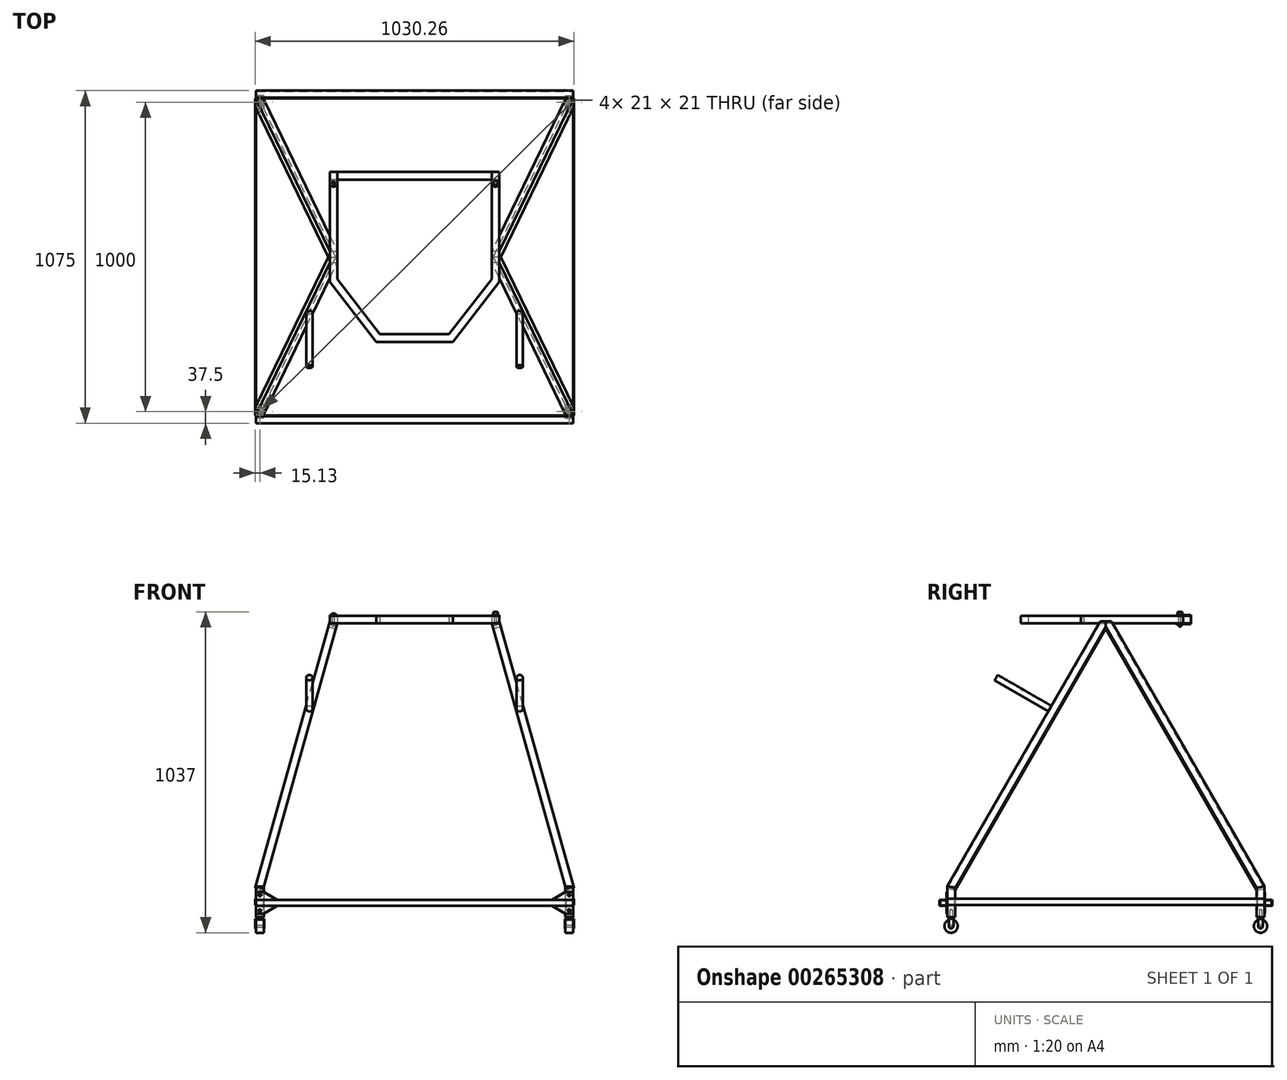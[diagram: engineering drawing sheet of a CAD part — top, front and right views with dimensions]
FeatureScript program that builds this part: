
annotation { "Feature Type Name" : "Feature", "Feature Type Description" : "" }
export const myFeature = defineFeature(function(context is Context, id is Id, definition is map)
    precondition{}
    {
        {
            assignVariable(context, id + "F0", {"name" : "Height", "anyValue" : 1000});
        }
        {
            var Q0;
            Q0=qCreatedBy(makeId("Top.planeOp"),FACE);
            var sketch = newSketch(context, id + "F1", { "sketchPlane" : qUnion([Q0])});
            skLineSegment(sketch, "E0.bottom", {"start": v(-487.5, 487.5) * mm, "end": v(-512.5, 487.5) * mm});
            skLineSegment(sketch, "E0.top", {"start": v(-487.5, 512.5) * mm, "end": v(-512.5, 512.5) * mm});
            skLineSegment(sketch, "E0.left", {"start": v(-487.5, 487.5) * mm, "end": v(-487.5, 512.5) * mm});
            skLineSegment(sketch, "E0.right", {"start": v(-512.5, 487.5) * mm, "end": v(-512.5, 512.5) * mm});
            skPoint(sketch, "E0.middle", {"position": v(-500, 500) * mm});
            skLineSegment(sketch, "E1.bottom", {"start": v(-489.5, 489.5) * mm, "end": v(-510.5, 489.5) * mm});
            skLineSegment(sketch, "E1.top", {"start": v(-489.5, 510.5) * mm, "end": v(-510.5, 510.5) * mm});
            skLineSegment(sketch, "E1.left", {"start": v(-489.5, 489.5) * mm, "end": v(-489.5, 510.5) * mm});
            skLineSegment(sketch, "E1.right", {"start": v(-510.5, 489.5) * mm, "end": v(-510.5, 510.5) * mm});
            skSolve(sketch);
        }
        {
            var Q0;
            Q0 = qSketchRegion(id + "F1", true);
            extrude(context, id + "F2", {"entities" : qUnion([Q0]), "depth" : 100 * mm});
        }
        {
            var Q0;
            Q0=makeQuery(id+"F2.opExtrude","SWEPT_BODY",BODY,{"disambiguationData":[OSD([sQuery(id+"F1.wireOp",EDGE,"E0.bottom"),sQuery(id+"F1.wireOp",EDGE,"E0.top"),sQuery(id+"F1.wireOp",EDGE,"E0.left"),sQuery(id+"F1.wireOp",EDGE,"E0.right"),sQuery(id+"F1.wireOp",EDGE,"E1.bottom"),sQuery(id+"F1.wireOp",EDGE,"E1.top"),sQuery(id+"F1.wireOp",EDGE,"E1.left"),sQuery(id+"F1.wireOp",EDGE,"E1.right")])]});
            var Q1;
            Q1=qCreatedBy(makeId("Front.planeOp"),FACE);
            mirror(context, id + "F3", {"entities" : qUnion([Q0]), "mirrorPlane" : qUnion([Q1])});
        }
        {
            var Q0;
            Q0=makeQuery(id+"F2.opExtrude","SWEPT_BODY",BODY,{"disambiguationData":[OSD([sQuery(id+"F1.wireOp",EDGE,"E0.bottom"),sQuery(id+"F1.wireOp",EDGE,"E0.top"),sQuery(id+"F1.wireOp",EDGE,"E0.left"),sQuery(id+"F1.wireOp",EDGE,"E0.right"),sQuery(id+"F1.wireOp",EDGE,"E1.bottom"),sQuery(id+"F1.wireOp",EDGE,"E1.top"),sQuery(id+"F1.wireOp",EDGE,"E1.left"),sQuery(id+"F1.wireOp",EDGE,"E1.right")])]});
            var Q1;
            Q1=makeQuery(id+"F3.opPattern","COPY",BODY,{"derivedFrom":makeQuery(id+"F2.opExtrude","SWEPT_BODY",BODY,{"disambiguationData":[OSD([sQuery(id+"F1.wireOp",EDGE,"E0.bottom"),sQuery(id+"F1.wireOp",EDGE,"E0.top"),sQuery(id+"F1.wireOp",EDGE,"E0.left"),sQuery(id+"F1.wireOp",EDGE,"E0.right"),sQuery(id+"F1.wireOp",EDGE,"E1.bottom"),sQuery(id+"F1.wireOp",EDGE,"E1.top"),sQuery(id+"F1.wireOp",EDGE,"E1.left"),sQuery(id+"F1.wireOp",EDGE,"E1.right")])]}),"instanceName":"1"});
            var Q2;
            Q2=qCreatedBy(makeId("Right.planeOp"),FACE);
            mirror(context, id + "F4", {"entities" : qUnion([Q0, Q1]), "mirrorPlane" : qUnion([Q2])});
        }
        {
            assignVariable(context, id + "F5", {"name" : "WheelHeight", "anyValue" : 50});
        }
        {
            var Q0;
            Q0=qCreatedBy(makeId("Top.planeOp"),FACE);
            cPlane(context, id + "F6", {"entities" : qUnion([Q0]), "cplaneType" : CPlaneType.OFFSET, "offset" : (getVariable(context, 'Height') - getVariable(context, 'WheelHeight')) * mm, "width" : 150 * mm, "height" : 150 * mm});
        }
        {
            var Q0;
            Q0=qCreatedBy(id+"F6.planeOp",FACE);
            var sketch = newSketch(context, id + "F7", { "sketchPlane" : qUnion([Q0])});
            skLineSegment(sketch, "E2", {"start": v(-250, 0) * mm, "end": v(250, 0) * mm, "construction": true});
            skSolve(sketch);
        }
        {
            var Q0;
            Q0=makeQuery(id+"F2.opExtrude","CAP_VERTEX",VERTEX,{"disambiguationData":[OSD([sQuery(id+"F1.wireOp",EDGE,"E0.bottom"),sQuery(id+"F1.wireOp",EDGE,"E0.left")])],"isStart":false});
            var Q1;
            Q1=makeQuery(id+"F3.opPattern","COPY",VERTEX,{"derivedFrom":makeQuery(id+"F2.opExtrude","CAP_VERTEX",VERTEX,{"disambiguationData":[OSD([sQuery(id+"F1.wireOp",EDGE,"E0.bottom"),sQuery(id+"F1.wireOp",EDGE,"E0.left")])],"isStart":false}),"instanceName":"1"});
            var Q2;
            Q2=sQuery(id+"F7.wireOp",VERTEX,"E2.start");
            cPlane(context, id + "F8", {"entities" : qUnion([Q0, Q1, Q2]), "cplaneType" : CPlaneType.THREE_POINT, "offset" : 25 * mm, "width" : 150 * mm, "height" : 150 * mm});
        }
        {
            var Q0;
            Q0=qCreatedBy(id+"F8.planeOp",FACE);
            var sketch = newSketch(context, id + "F9", { "sketchPlane" : qUnion([Q0])});
            skLineSegment(sketch, "E3", {"start": v(512.5, -41.6) * mm, "end": v(18.38, 847.68) * mm});
            skLineSegment(sketch, "E4", {"start": v(18.38, 847.68) * mm, "end": v(0, 847.68) * mm});
            skLineSegment(sketch, "E5", {"start": v(0, 847.68) * mm, "end": v(0, 829.3) * mm});
            skLineSegment(sketch, "E6", {"start": v(0, 829.3) * mm, "end": v(487.5, -48.08) * mm});
            skLineSegment(sketch, "E7", {"start": v(487.5, -48.08) * mm, "end": v(512.5, -41.6) * mm});
            skSolve(sketch);
        }
        {
            var Q0;
            Q0 = qSketchRegion(id + "F9", true);
            extrude(context, id + "F10", {"entities" : qUnion([Q0]), "oppositeDirection" : true, "depth" : 25 * mm});
        }
        {
            var Q0;
            Q0=makeQuery(id+"F10.opExtrude","SWEPT_BODY",BODY,{"disambiguationData":[OSD([sQuery(id+"F9.wireOp",EDGE,"E3"),sQuery(id+"F9.wireOp",EDGE,"E4"),sQuery(id+"F9.wireOp",EDGE,"E5"),sQuery(id+"F9.wireOp",EDGE,"E6"),sQuery(id+"F9.wireOp",EDGE,"E7")])]});
            var Q1;
            Q1=qCreatedBy(makeId("Front.planeOp"),FACE);
            mirror(context, id + "F11", {"entities" : qUnion([Q0]), "mirrorPlane" : qUnion([Q1])});
        }
        {
            var Q0;
            Q0=makeQuery(id+"F10.opExtrude","SWEPT_BODY",BODY,{"disambiguationData":[OSD([sQuery(id+"F9.wireOp",EDGE,"E3"),sQuery(id+"F9.wireOp",EDGE,"E4"),sQuery(id+"F9.wireOp",EDGE,"E5"),sQuery(id+"F9.wireOp",EDGE,"E6"),sQuery(id+"F9.wireOp",EDGE,"E7")])]});
            var Q1;
            Q1=makeQuery(id+"F11.opPattern","COPY",BODY,{"derivedFrom":makeQuery(id+"F10.opExtrude","SWEPT_BODY",BODY,{"disambiguationData":[OSD([sQuery(id+"F9.wireOp",EDGE,"E3"),sQuery(id+"F9.wireOp",EDGE,"E4"),sQuery(id+"F9.wireOp",EDGE,"E5"),sQuery(id+"F9.wireOp",EDGE,"E6"),sQuery(id+"F9.wireOp",EDGE,"E7")])]}),"instanceName":"1"});
            var Q2;
            Q2=qCreatedBy(makeId("Right.planeOp"),FACE);
            mirror(context, id + "F12", {"entities" : qUnion([Q0, Q1]), "mirrorPlane" : qUnion([Q2])});
        }
        {
            var Q0;
            Q0=makeQuery(id+"F2.opExtrude","SWEPT_FACE",FACE,{"disambiguationData":[OSD([sQuery(id+"F1.wireOp",EDGE,"E0.right")])]});
            var sketch = newSketch(context, id + "F13", { "sketchPlane" : qUnion([Q0])});
            skLineSegment(sketch, "E8.bottom", {"start": v(512.5, 40) * mm, "end": v(-512.5, 40) * mm});
            skLineSegment(sketch, "E8.top", {"start": v(512.5, 60) * mm, "end": v(-512.5, 60) * mm});
            skLineSegment(sketch, "E8.left", {"start": v(512.5, 40) * mm, "end": v(512.5, 60) * mm});
            skLineSegment(sketch, "E8.right", {"start": v(-512.5, 40) * mm, "end": v(-512.5, 60) * mm});
            skPoint(sketch, "E8.middle", {"position": v(0, 50) * mm});
            skPoint(sketch, "E8.middle.positionSnap0", {"position": v(-487.5, 50) * mm});
            skPoint(sketch, "E8.centerSnap0", {"position": v(-487.5, 50) * mm});
            skPoint(sketch, "E9.centerSnap0", {"position": v(-500, 0) * mm});
            skSolve(sketch);
        }
        {
            var Q0;
            Q0 = qSketchRegion(id + "F13", true);
            extrude(context, id + "F14", {"entities" : qUnion([Q0]), "depth" : 2 * mm});
        }
        {
            var Q0;
            Q0=makeQuery(id+"F14.opExtrude","SWEPT_BODY",BODY,{"disambiguationData":[OSD([sQuery(id+"F13.wireOp",EDGE,"E8.bottom"),sQuery(id+"F13.wireOp",EDGE,"E8.top"),sQuery(id+"F13.wireOp",EDGE,"E8.left"),sQuery(id+"F13.wireOp",EDGE,"E8.right")])]});
            var Q1;
            Q1=qCreatedBy(makeId("Right.planeOp"),FACE);
            mirror(context, id + "F15", {"entities" : qUnion([Q0]), "mirrorPlane" : qUnion([Q1])});
        }
        {
            var Q0;
            Q0=qCreatedBy(makeId("Top.planeOp"),FACE);
            var sketch = newSketch(context, id + "F16", { "sketchPlane" : qUnion([Q0])});
            skCircle(sketch, "E10", {"center": v(-500, -500) * mm, "radius": 4 * mm});
            skLineSegment(sketch, "E11", {"start": v(-519.3, -500) * mm, "end": v(-467.5, -500) * mm, "construction": true});
            skLineSegment(sketch, "E12", {"start": v(-500, -518.88) * mm, "end": v(-500, -479.27) * mm, "construction": true});
            skSolve(sketch);
        }
        {
            var Q0;
            Q0 = qSketchRegion(id + "F16", true);
            extrude(context, id + "F17", {"entities" : qUnion([Q0]), "depth" : 25 * mm, "hasSecondDirection" : true, "secondDirectionOppositeDirection" : true, "secondDirectionDepth" : 5 * mm});
        }
        {
            var Q0;
            Q0=makeQuery(id+"F17.opExtrude","CAP_FACE",FACE,{"disambiguationData":[OSD([sQuery(id+"F16.wireOp",EDGE,"E10")])],"isStart":true});
            var sketch = newSketch(context, id + "F18", { "sketchPlane" : qUnion([Q0])});
            skLineSegment(sketch, "E13.bottom", {"start": v(-487.5, 492.5) * mm, "end": v(-512.5, 492.5) * mm});
            skLineSegment(sketch, "E13.top", {"start": v(-487.5, 507.5) * mm, "end": v(-512.5, 507.5) * mm});
            skLineSegment(sketch, "E13.left", {"start": v(-487.5, 492.5) * mm, "end": v(-487.5, 507.5) * mm});
            skLineSegment(sketch, "E13.right", {"start": v(-512.5, 492.5) * mm, "end": v(-512.5, 507.5) * mm});
            skPoint(sketch, "E13.middle", {"position": v(-500, 500) * mm});
            skSolve(sketch);
        }
        {
            var Q0;
            Q0 = qSketchRegion(id + "F18", true);
            extrude(context, id + "F19", {"entities" : qUnion([Q0]), "operationType" : NewBodyOperationType.ADD, "depth" : 2 * mm});
        }
        {
            var Q0;
            Q0=makeQuery(id+"F19.opExtrude","SWEPT_FACE",FACE,{"disambiguationData":[OSD([sQuery(id+"F18.wireOp",EDGE,"E13.left")])]});
            var sketch = newSketch(context, id + "F20", { "sketchPlane" : qUnion([Q0])});
            skLineSegment(sketch, "E14", {"start": v(-507.5, -5) * mm, "end": v(-507.5, -28.5) * mm});
            skLineSegment(sketch, "E15", {"start": v(-507.5, -5) * mm, "end": v(-492.5, -5) * mm});
            skLineSegment(sketch, "E16", {"start": v(-492.5, -5) * mm, "end": v(-492.5, -28.5) * mm});
            skCircle(sketch, "E17", {"center": v(-500, -28.5) * mm, "radius": 3 * mm});
            skPoint(sketch, "E17.centerSnap0", {"position": v(-500, -7) * mm});
            skArc(sketch, "E18", {"start": v(-507.5, -28.5) * mm, "mid": v(-500, -36) * mm, "end": v(-492.5, -28.5) * mm});
            skSolve(sketch);
        }
        {
            var Q0;
            Q0 = qSketchRegion(id + "F20", true);
            extrude(context, id + "F21", {"entities" : qUnion([Q0]), "depth" : 2 * mm});
        }
        {
            var Q0;
            Q0=makeQuery(id+"F3.opPattern","COPY",FACE,{"derivedFrom":makeQuery(id+"F2.opExtrude","SWEPT_FACE",FACE,{"disambiguationData":[OSD([sQuery(id+"F1.wireOp",EDGE,"E0.left")])]}),"instanceName":"1"});
            var Q1;
            Q1=makeQuery(id+"F3.opPattern","COPY",FACE,{"derivedFrom":makeQuery(id+"F2.opExtrude","SWEPT_FACE",FACE,{"disambiguationData":[OSD([sQuery(id+"F1.wireOp",EDGE,"E0.right")])]}),"instanceName":"1"});
            cPlane(context, id + "F22", {"entities" : qUnion([Q0, Q1]), "cplaneType" : CPlaneType.MID_PLANE, "offset" : 25 * mm, "width" : 150 * mm, "height" : 150 * mm});
        }
        {
            var Q0;
            Q0=makeQuery(id+"F21.opExtrude","SWEPT_BODY",BODY,{"disambiguationData":[OSD([sQuery(id+"F20.wireOp",EDGE,"E14"),sQuery(id+"F20.wireOp",EDGE,"E15"),sQuery(id+"F20.wireOp",EDGE,"E16"),sQuery(id+"F20.wireOp",EDGE,"E17"),sQuery(id+"F20.wireOp",EDGE,"E18")])]});
            var Q1;
            Q1=qCreatedBy(id+"F22.planeOp",FACE);
            mirror(context, id + "F23", {"operationType" : NewBodyOperationType.ADD, "entities" : qUnion([Q0]), "mirrorPlane" : qUnion([Q1])});
        }
        {
            var Q0;
            Q0=makeQuery(id+"F21.opExtrude","CAP_FACE",FACE,{"disambiguationData":[OSD([sQuery(id+"F20.wireOp",EDGE,"E14"),sQuery(id+"F20.wireOp",EDGE,"E15"),sQuery(id+"F20.wireOp",EDGE,"E16"),sQuery(id+"F20.wireOp",EDGE,"E17"),sQuery(id+"F20.wireOp",EDGE,"E18")])],"isStart":false});
            var sketch = newSketch(context, id + "F24", { "sketchPlane" : qUnion([Q0])});
            skCircle(sketch, "E19.0", {"center": v(-500, -28.5) * mm, "radius": 3 * mm});
            skSolve(sketch);
        }
        {
            var Q0;
            Q0 = qSketchRegion(id + "F24", true);
            var Q1;
            Q1=makeQuery(id+"F23.opPattern","COPY",FACE,{"derivedFrom":makeQuery(id+"F21.opExtrude","CAP_FACE",FACE,{"disambiguationData":[OSD([sQuery(id+"F20.wireOp",EDGE,"E14"),sQuery(id+"F20.wireOp",EDGE,"E15"),sQuery(id+"F20.wireOp",EDGE,"E16"),sQuery(id+"F20.wireOp",EDGE,"E17"),sQuery(id+"F20.wireOp",EDGE,"E18")])],"isStart":false}),"instanceName":"1"});
            extrude(context, id + "F25", {"entities" : qUnion([Q0]), "operationType" : NewBodyOperationType.ADD, "endBound" : BoundingType.UP_TO_SURFACE, "oppositeDirection" : true, "endBoundEntityFace" : qUnion([Q1]), "depth" : 25 * mm});
        }
        {
            var Q0;
            Q0=makeQuery(id+"F23.opPattern","COPY",FACE,{"derivedFrom":makeQuery(id+"F21.opExtrude","CAP_FACE",FACE,{"disambiguationData":[OSD([sQuery(id+"F20.wireOp",EDGE,"E14"),sQuery(id+"F20.wireOp",EDGE,"E15"),sQuery(id+"F20.wireOp",EDGE,"E16"),sQuery(id+"F20.wireOp",EDGE,"E17"),sQuery(id+"F20.wireOp",EDGE,"E18")])],"isStart":true}),"instanceName":"1"});
            var sketch = newSketch(context, id + "F26", { "sketchPlane" : qUnion([Q0])});
            skCircle(sketch, "E20.0", {"center": v(-500, -28.5) * mm, "radius": 3 * mm});
            skCircle(sketch, "E21", {"center": v(-500, -28.5) * mm, "radius": 21.5 * mm});
            skSolve(sketch);
        }
        {
            var Q0;
            Q0 = qSketchRegion(id + "F26", true);
            extrude(context, id + "F27", {"entities" : qUnion([Q0]), "depth" : 25 * mm});
        }
        {
            var Q0;
            Q0=makeQuery(id+"F27.opExtrude","SWEPT_BODY",BODY,{"disambiguationData":[OSD([sQuery(id+"F26.wireOp",EDGE,"E20.0"),sQuery(id+"F26.wireOp",EDGE,"E21")])]});
            var Q1;
            Q1=makeQuery(id+"F17.opExtrude","SWEPT_BODY",BODY,{"disambiguationData":[OSD([sQuery(id+"F16.wireOp",EDGE,"E10")])]});
            var Q2;
            Q2=qCreatedBy(makeId("Right.planeOp"),FACE);
            mirror(context, id + "F28", {"entities" : qUnion([Q0, Q1]), "mirrorPlane" : qUnion([Q2])});
        }
        {
            var Q0;
            Q0=makeQuery(id+"F27.opExtrude","SWEPT_BODY",BODY,{"disambiguationData":[OSD([sQuery(id+"F26.wireOp",EDGE,"E20.0"),sQuery(id+"F26.wireOp",EDGE,"E21")])]});
            var Q1;
            Q1=makeQuery(id+"F17.opExtrude","SWEPT_BODY",BODY,{"disambiguationData":[OSD([sQuery(id+"F16.wireOp",EDGE,"E10")])]});
            var Q2;
            Q2=makeQuery(id+"F28.opPattern","COPY",BODY,{"derivedFrom":makeQuery(id+"F27.opExtrude","SWEPT_BODY",BODY,{"disambiguationData":[OSD([sQuery(id+"F26.wireOp",EDGE,"E20.0"),sQuery(id+"F26.wireOp",EDGE,"E21")])]}),"instanceName":"1"});
            var Q3;
            Q3=makeQuery(id+"F28.opPattern","COPY",BODY,{"derivedFrom":makeQuery(id+"F17.opExtrude","SWEPT_BODY",BODY,{"disambiguationData":[OSD([sQuery(id+"F16.wireOp",EDGE,"E10")])]}),"instanceName":"1"});
            var Q4;
            Q4=qCreatedBy(makeId("Front.planeOp"),FACE);
            mirror(context, id + "F29", {"entities" : qUnion([Q0, Q1, Q2, Q3]), "mirrorPlane" : qUnion([Q4])});
        }
        {
            var Q0;
            Q0=makeQuery(id+"F3.opPattern","COPY",FACE,{"derivedFrom":makeQuery(id+"F2.opExtrude","SWEPT_FACE",FACE,{"disambiguationData":[OSD([sQuery(id+"F1.wireOp",EDGE,"E0.top")])]}),"instanceName":"1"});
            var sketch = newSketch(context, id + "F30", { "sketchPlane" : qUnion([Q0])});
            skLineSegment(sketch, "E22", {"start": v(-512.5, 81.8) * mm, "end": v(-512.5, 11.8) * mm});
            skLineSegment(sketch, "E23", {"start": v(-512.5, 11.8) * mm, "end": v(-487.5, 11.8) * mm});
            skLineSegment(sketch, "E24", {"start": v(-487.5, 11.8) * mm, "end": v(-444.2, 36.8) * mm});
            skLineSegment(sketch, "E25", {"start": v(-444.2, 36.8) * mm, "end": v(444.2, 36.8) * mm});
            skLineSegment(sketch, "E26", {"start": v(444.2, 36.8) * mm, "end": v(487.5, 11.8) * mm});
            skLineSegment(sketch, "E27", {"start": v(487.5, 11.8) * mm, "end": v(512.5, 11.8) * mm});
            skLineSegment(sketch, "E28", {"start": v(512.5, 11.8) * mm, "end": v(512.5, 81.8) * mm});
            skLineSegment(sketch, "E29", {"start": v(512.5, 81.8) * mm, "end": v(487.5, 81.8) * mm});
            skLineSegment(sketch, "E30", {"start": v(487.5, 81.8) * mm, "end": v(444.2, 56.8) * mm});
            skLineSegment(sketch, "E31", {"start": v(444.2, 56.8) * mm, "end": v(-444.2, 56.8) * mm});
            skLineSegment(sketch, "E32", {"start": v(-444.2, 56.8) * mm, "end": v(-487.5, 81.8) * mm});
            skLineSegment(sketch, "E33", {"start": v(-487.5, 81.8) * mm, "end": v(-512.5, 81.8) * mm});
            skCircle(sketch, "E34", {"center": v(-500, 71.8) * mm, "radius": 4 * mm});
            skPoint(sketch, "E34.centerSnap0", {"position": v(-500, 81.8) * mm});
            skCircle(sketch, "E35", {"center": v(-500, 21.8) * mm, "radius": 4 * mm});
            skPoint(sketch, "E35.centerSnap0", {"position": v(-500, 11.8) * mm});
            skCircle(sketch, "E36", {"center": v(500, 71.8) * mm, "radius": 4 * mm});
            skPoint(sketch, "E36.centerSnap0", {"position": v(500, 81.8) * mm});
            skCircle(sketch, "E37", {"center": v(500, 21.8) * mm, "radius": 4 * mm});
            skPoint(sketch, "E37.centerSnap0", {"position": v(500, 11.8) * mm});
            skSolve(sketch);
        }
        {
            var Q0;
            Q0 = qSketchRegion(id + "F30", true);
            extrude(context, id + "F31", {"entities" : qUnion([Q0]), "depth" : 2 * mm});
        }
        {
            var Q0;
            Q0=makeQuery(id+"F31.opExtrude","SWEPT_BODY",BODY,{"disambiguationData":[OSD([sQuery(id+"F30.wireOp",EDGE,"E22"),sQuery(id+"F30.wireOp",EDGE,"E23"),sQuery(id+"F30.wireOp",EDGE,"E24"),sQuery(id+"F30.wireOp",EDGE,"E25"),sQuery(id+"F30.wireOp",EDGE,"E26"),sQuery(id+"F30.wireOp",EDGE,"E27"),sQuery(id+"F30.wireOp",EDGE,"E28"),sQuery(id+"F30.wireOp",EDGE,"E29"),sQuery(id+"F30.wireOp",EDGE,"E30"),sQuery(id+"F30.wireOp",EDGE,"E31"),sQuery(id+"F30.wireOp",EDGE,"E32"),sQuery(id+"F30.wireOp",EDGE,"E33"),sQuery(id+"F30.wireOp",EDGE,"E34"),sQuery(id+"F30.wireOp",EDGE,"E35"),sQuery(id+"F30.wireOp",EDGE,"E36"),sQuery(id+"F30.wireOp",EDGE,"E37")])]});
            var Q1;
            Q1=qCreatedBy(makeId("Front.planeOp"),FACE);
            mirror(context, id + "F32", {"entities" : qUnion([Q0]), "mirrorPlane" : qUnion([Q1])});
        }
        {
            var Q0;
            Q0=makeQuery(id+"F31.opExtrude","CAP_FACE",FACE,{"disambiguationData":[OSD([sQuery(id+"F30.wireOp",EDGE,"E22"),sQuery(id+"F30.wireOp",EDGE,"E23"),sQuery(id+"F30.wireOp",EDGE,"E24"),sQuery(id+"F30.wireOp",EDGE,"E25"),sQuery(id+"F30.wireOp",EDGE,"E26"),sQuery(id+"F30.wireOp",EDGE,"E27"),sQuery(id+"F30.wireOp",EDGE,"E28"),sQuery(id+"F30.wireOp",EDGE,"E29"),sQuery(id+"F30.wireOp",EDGE,"E30"),sQuery(id+"F30.wireOp",EDGE,"E31"),sQuery(id+"F30.wireOp",EDGE,"E32"),sQuery(id+"F30.wireOp",EDGE,"E33"),sQuery(id+"F30.wireOp",EDGE,"E34"),sQuery(id+"F30.wireOp",EDGE,"E35"),sQuery(id+"F30.wireOp",EDGE,"E36"),sQuery(id+"F30.wireOp",EDGE,"E37")])],"isStart":false});
            var sketch = newSketch(context, id + "F33", { "sketchPlane" : qUnion([Q0])});
            skLineSegment(sketch, "E38.bottom", {"start": v(-512.5, 56.8) * mm, "end": v(512.5, 56.8) * mm});
            skLineSegment(sketch, "E38.top", {"start": v(-512.5, 36.8) * mm, "end": v(512.5, 36.8) * mm});
            skLineSegment(sketch, "E38.left", {"start": v(-512.5, 56.8) * mm, "end": v(-512.5, 36.8) * mm});
            skLineSegment(sketch, "E38.right", {"start": v(512.5, 56.8) * mm, "end": v(512.5, 36.8) * mm});
            skSolve(sketch);
        }
        {
            var Q0;
            Q0 = qSketchRegion(id + "F33", true);
            extrude(context, id + "F34", {"entities" : qUnion([Q0]), "depth" : 23 * mm, "hasSecondDirection" : true, "secondDirectionOppositeDirection" : true, "secondDirectionDepth" : 2 * mm});
        }
        {
            var Q0;
            Q0=makeQuery(id+"F34.opExtrude","SWEPT_FACE",FACE,{"disambiguationData":[OSD([sQuery(id+"F33.wireOp",EDGE,"E38.left")])]});
            var Q1;
            Q1=makeQuery(id+"F34.opExtrude","SWEPT_FACE",FACE,{"disambiguationData":[OSD([sQuery(id+"F33.wireOp",EDGE,"E38.right")])]});
            shell(context, id + "F35", {"entities" : qUnion([Q0, Q1]), "thickness" : 2 * mm});
        }
        {
            var Q0;
            Q0=makeQuery(id+"F34.opExtrude","SWEPT_BODY",BODY,{"disambiguationData":[OSD([sQuery(id+"F33.wireOp",EDGE,"E38.bottom"),sQuery(id+"F33.wireOp",EDGE,"E38.top"),sQuery(id+"F33.wireOp",EDGE,"E38.left"),sQuery(id+"F33.wireOp",EDGE,"E38.right")])]});
            var Q1;
            Q1=qCreatedBy(makeId("Front.planeOp"),FACE);
            mirror(context, id + "F36", {"entities" : qUnion([Q0]), "mirrorPlane" : qUnion([Q1])});
        }
        {
            var Q0;
            Q0=makeQuery(id+"F3.opPattern","COPY",VERTEX,{"derivedFrom":makeQuery(id+"F2.opExtrude","CAP_VERTEX",VERTEX,{"disambiguationData":[OSD([sQuery(id+"F1.wireOp",EDGE,"E0.top"),sQuery(id+"F1.wireOp",EDGE,"E0.right")])],"isStart":false}),"instanceName":"1"});
            var Q1;
            Q1=makeQuery(id+"F12.opPattern","COPY",VERTEX,{"derivedFrom":makeQuery(id+"F11.opPattern","COPY",VERTEX,{"derivedFrom":makeQuery(id+"F10.opExtrude","CAP_VERTEX",VERTEX,{"disambiguationData":[OSD([sQuery(id+"F9.wireOp",EDGE,"E3"),sQuery(id+"F9.wireOp",EDGE,"E7")])],"isStart":false}),"instanceName":"1"}),"instanceName":"1"});
            var Q2;
            Q2=makeQuery(id+"F11.opPattern","COPY",VERTEX,{"derivedFrom":makeQuery(id+"F10.opExtrude","CAP_VERTEX",VERTEX,{"disambiguationData":[OSD([sQuery(id+"F9.wireOp",EDGE,"E3"),sQuery(id+"F9.wireOp",EDGE,"E4")])],"isStart":false}),"instanceName":"1"});
            cPlane(context, id + "F37", {"entities" : qUnion([Q0, Q1, Q2]), "cplaneType" : CPlaneType.THREE_POINT, "offset" : 25 * mm, "width" : 150 * mm, "height" : 150 * mm});
        }
        {
            var Q0;
            Q0=qCreatedBy(id+"F37.planeOp",FACE);
            var sketch = newSketch(context, id + "F38", { "sketchPlane" : qUnion([Q0])});
            skCircle(sketch, "E39", {"center": v(-339.9, 494.04) * mm, "radius": 10 * mm});
            skCircle(sketch, "E40", {"center": v(339.78, 494.04) * mm, "radius": 10 * mm});
            skSolve(sketch);
        }
        {
            var Q0;
            Q0 = qSketchRegion(id + "F38", true);
            var Q1;
            Q1=makeQuery(id+"F10.opExtrude","SWEPT_FACE",FACE,{"disambiguationData":[OSD([sQuery(id+"F9.wireOp",EDGE,"E3")])]});
            extrude(context, id + "F39", {"entities" : qUnion([Q0]), "oppositeDirection" : true, "depth" : 200 * mm, "hasSecondDirection" : true, "secondDirectionBound" : SecondDirectionBoundingType.UP_TO_NEXT, "secondDirectionOppositeDirection" : false, "secondDirectionBoundEntityFace" : qUnion([Q1]), "secondDirectionDepth" : 25 * mm});
        }
        {
            var Q0;
            Q0=qCreatedBy(id+"F6.planeOp",FACE);
            var sketch = newSketch(context, id + "F40", { "sketchPlane" : qUnion([Q0])});
            skLineSegment(sketch, "E41.bottom", {"start": v(-274.08, 250) * mm, "end": v(-249.08, 250) * mm});
            skLineSegment(sketch, "E41.top", {"start": v(-274.08, -80) * mm, "end": v(-249.08, -80) * mm});
            skLineSegment(sketch, "E41.left", {"start": v(-274.08, 250) * mm, "end": v(-274.08, -80) * mm});
            skLineSegment(sketch, "E41.right", {"start": v(-249.08, 250) * mm, "end": v(-249.08, -80) * mm});
            skLineSegment(sketch, "E42.bottom", {"start": v(249.08, 250) * mm, "end": v(274.08, 250) * mm});
            skLineSegment(sketch, "E42.top", {"start": v(249.08, -80) * mm, "end": v(274.08, -80) * mm});
            skLineSegment(sketch, "E42.left", {"start": v(249.08, 250) * mm, "end": v(249.08, -80) * mm});
            skLineSegment(sketch, "E42.right", {"start": v(274.08, 250) * mm, "end": v(274.08, -80) * mm});
            skLineSegment(sketch, "E43.bottom", {"start": v(123.93, -275) * mm, "end": v(-123.93, -275) * mm});
            skLineSegment(sketch, "E43.top", {"start": v(123.93, -250) * mm, "end": v(-123.93, -250) * mm});
            skLineSegment(sketch, "E43.left", {"start": v(123.93, -275) * mm, "end": v(123.93, -250) * mm});
            skLineSegment(sketch, "E43.right", {"start": v(-123.93, -275) * mm, "end": v(-123.93, -250) * mm});
            skLineSegment(sketch, "E44", {"start": v(123.93, -275) * mm, "end": v(274.08, -80) * mm});
            skLineSegment(sketch, "E45", {"start": v(111.63, -250) * mm, "end": v(249.08, -71.5) * mm});
            skLineSegment(sketch, "E46", {"start": v(-123.93, -275) * mm, "end": v(-274.08, -80) * mm});
            skLineSegment(sketch, "E47", {"start": v(-111.63, -250) * mm, "end": v(-249.08, -71.5) * mm});
            skSolve(sketch);
        }
        {
            var Q0;
            Q0 = qSketchRegion(id + "F40", true);
            extrude(context, id + "F41", {"entities" : qUnion([Q0]), "depth" : 25 * mm});
        }
        {
            var Q0;
            Q0=qCreatedBy(id+"F6.planeOp",FACE);
            var sketch = newSketch(context, id + "F42", { "sketchPlane" : qUnion([Q0])});
            skLineSegment(sketch, "E48.bottom", {"start": v(274.08, 250) * mm, "end": v(-274.08, 250) * mm});
            skLineSegment(sketch, "E48.top", {"start": v(274.08, 275) * mm, "end": v(-274.08, 275) * mm});
            skLineSegment(sketch, "E48.left", {"start": v(274.08, 250) * mm, "end": v(274.08, 275) * mm});
            skLineSegment(sketch, "E48.right", {"start": v(-274.08, 250) * mm, "end": v(-274.08, 275) * mm});
            skSolve(sketch);
        }
        {
            var Q0;
            Q0 = qSketchRegion(id + "F42", true);
            extrude(context, id + "F43", {"entities" : qUnion([Q0]), "depth" : 25 * mm});
        }
        {
            var Q0;
            Q0=makeQuery(id+"F43.opExtrude","CAP_FACE",FACE,{"disambiguationData":[OSD([sQuery(id+"F42.wireOp",EDGE,"E48.bottom"),sQuery(id+"F42.wireOp",EDGE,"E48.top"),sQuery(id+"F42.wireOp",EDGE,"E48.left"),sQuery(id+"F42.wireOp",EDGE,"E48.right")])],"isStart":false});
            var sketch = newSketch(context, id + "F44", { "sketchPlane" : qUnion([Q0])});
            skArc(sketch, "E49", {"start": v(-249.08, 239.3) * mm, "mid": v(-261.58, 226.8) * mm, "end": v(-274.08, 239.3) * mm});
            skLineSegment(sketch, "E50", {"start": v(-249.08, 239.3) * mm, "end": v(-249.08, 275) * mm});
            skLineSegment(sketch, "E51", {"start": v(-249.08, 275) * mm, "end": v(-274.08, 275) * mm});
            skLineSegment(sketch, "E52", {"start": v(-274.08, 275) * mm, "end": v(-274.08, 239.3) * mm});
            skSolve(sketch);
        }
        {
            var Q0;
            Q0 = qSketchRegion(id + "F44", true);
            extrude(context, id + "F45", {"entities" : qUnion([Q0]), "depth" : 2 * mm});
        }
        {
            var Q0;
            Q0=makeQuery(id+"F45.opExtrude","SWEPT_BODY",BODY,{"disambiguationData":[OSD([sQuery(id+"F44.wireOp",EDGE,"E49"),sQuery(id+"F44.wireOp",EDGE,"E50"),sQuery(id+"F44.wireOp",EDGE,"E51"),sQuery(id+"F44.wireOp",EDGE,"E52")])]});
            var Q1;
            Q1=makeQuery(id+"F43.opExtrude","SWEPT_EDGE",EDGE,{"disambiguationData":[OSD([sQuery(id+"F42.wireOp",EDGE,"E48.top"),sQuery(id+"F42.wireOp",EDGE,"E48.right")])]});
            var Q2;
            Q2=makeQuery(id+"F43.opExtrude","SWEPT_EDGE",EDGE,{"disambiguationData":[OSD([sQuery(id+"F42.wireOp",EDGE,"E48.top"),sQuery(id+"F42.wireOp",EDGE,"E48.right")])]});
            transform(context, id + "F46", {"entities" : qUnion([Q0]), "transformType" : TransformType.TRANSLATION_DISTANCE, "transformDirection" : qUnion([Q2]), "distance" : (25 + 2) * mm, "makeCopy" : true});
        }
        {
            var Q0;
            Q0=makeQuery(id+"F45.opExtrude","CAP_FACE",FACE,{"disambiguationData":[OSD([sQuery(id+"F44.wireOp",EDGE,"E49"),sQuery(id+"F44.wireOp",EDGE,"E50"),sQuery(id+"F44.wireOp",EDGE,"E51"),sQuery(id+"F44.wireOp",EDGE,"E52")])],"isStart":false});
            var sketch = newSketch(context, id + "F47", { "sketchPlane" : qUnion([Q0])});
            skCircle(sketch, "E53", {"center": v(-261.58, 239.3) * mm, "radius": 3 * mm});
            skSolve(sketch);
        }
        {
            var Q0;
            Q0 = qSketchRegion(id + "F47", true);
            extrude(context, id + "F48", {"entities" : qUnion([Q0]), "oppositeDirection" : true, "depth" : (25 + 2 + 2 + 8) * mm});
        }
        {
            var Q0;
            Q0=makeQuery(id+"F45.opExtrude","CAP_FACE",FACE,{"disambiguationData":[OSD([sQuery(id+"F44.wireOp",EDGE,"E49"),sQuery(id+"F44.wireOp",EDGE,"E50"),sQuery(id+"F44.wireOp",EDGE,"E51"),sQuery(id+"F44.wireOp",EDGE,"E52")])],"isStart":false});
            var sketch = newSketch(context, id + "F49", { "sketchPlane" : qUnion([Q0])});
            skCircle(sketch, "E54.cCircle", {"center": v(-261.58, 239.3) * mm, "radius": 5 * mm, "construction": true});
            skLineSegment(sketch, "E54.0", {"start": v(-266.76, 241.84) * mm, "end": v(-261.96, 245.05) * mm});
            skLineSegment(sketch, "E54.1", {"start": v(-261.96, 245.05) * mm, "end": v(-256.78, 242.5) * mm});
            skLineSegment(sketch, "E54.2", {"start": v(-256.78, 242.5) * mm, "end": v(-256.4, 236.75) * mm});
            skLineSegment(sketch, "E54.3", {"start": v(-256.4, 236.75) * mm, "end": v(-261.2, 233.53) * mm});
            skLineSegment(sketch, "E54.4", {"start": v(-261.2, 233.53) * mm, "end": v(-266.37, 236.08) * mm});
            skLineSegment(sketch, "E54.5", {"start": v(-266.37, 236.08) * mm, "end": v(-266.76, 241.84) * mm});
            skPoint(sketch, "E54.0.midPoint", {"position": v(-264.36, 243.45) * mm});
            skSolve(sketch);
        }
        {
            var Q0;
            Q0 = qSketchRegion(id + "F49", true);
            extrude(context, id + "F50", {"entities" : qUnion([Q0]), "operationType" : NewBodyOperationType.ADD, "depth" : 5 * mm});
        }
        {
            var Q0;
            Q0=makeQuery(id+"F46.opPattern","COPY",FACE,{"derivedFrom":makeQuery(id+"F45.opExtrude","CAP_FACE",FACE,{"disambiguationData":[OSD([sQuery(id+"F44.wireOp",EDGE,"E49"),sQuery(id+"F44.wireOp",EDGE,"E50"),sQuery(id+"F44.wireOp",EDGE,"E51"),sQuery(id+"F44.wireOp",EDGE,"E52")])],"isStart":true}),"instanceName":"1"});
            var sketch = newSketch(context, id + "F51", { "sketchPlane" : qUnion([Q0])});
            skCircle(sketch, "E55.0.0", {"center": v(-261.58, -239.3) * mm, "radius": 3 * mm});
            skCircle(sketch, "E56.cCircle", {"center": v(-261.58, -239.3) * mm, "radius": 5 * mm, "construction": true});
            skLineSegment(sketch, "E56.0", {"start": v(-255.83, -238.74) * mm, "end": v(-258.23, -244) * mm});
            skLineSegment(sketch, "E56.1", {"start": v(-258.23, -244) * mm, "end": v(-263.97, -244.55) * mm});
            skLineSegment(sketch, "E56.2", {"start": v(-263.97, -244.55) * mm, "end": v(-267.32, -239.84) * mm});
            skLineSegment(sketch, "E56.3", {"start": v(-267.32, -239.84) * mm, "end": v(-264.93, -234.6) * mm});
            skLineSegment(sketch, "E56.4", {"start": v(-264.93, -234.6) * mm, "end": v(-259.18, -234.04) * mm});
            skLineSegment(sketch, "E56.5", {"start": v(-259.18, -234.04) * mm, "end": v(-255.83, -238.74) * mm});
            skPoint(sketch, "E56.0.midPoint", {"position": v(-257.03, -241.37) * mm});
            skSolve(sketch);
        }
        {
            var Q0;
            Q0 = qSketchRegion(id + "F51", true);
            extrude(context, id + "F52", {"entities" : qUnion([Q0]), "depth" : 5 * mm});
        }
        {
            var Q0;
            Q0=makeQuery(id+"F45.opExtrude","SWEPT_BODY",BODY,{"disambiguationData":[OSD([sQuery(id+"F44.wireOp",EDGE,"E49"),sQuery(id+"F44.wireOp",EDGE,"E50"),sQuery(id+"F44.wireOp",EDGE,"E51"),sQuery(id+"F44.wireOp",EDGE,"E52")])]});
            var Q1;
            Q1=makeQuery(id+"F46.opPattern","COPY",BODY,{"derivedFrom":makeQuery(id+"F45.opExtrude","SWEPT_BODY",BODY,{"disambiguationData":[OSD([sQuery(id+"F44.wireOp",EDGE,"E49"),sQuery(id+"F44.wireOp",EDGE,"E50"),sQuery(id+"F44.wireOp",EDGE,"E51"),sQuery(id+"F44.wireOp",EDGE,"E52")])]}),"instanceName":"1"});
            var Q2;
            Q2=qCreatedBy(makeId("Right.planeOp"),FACE);
            mirror(context, id + "F53", {"entities" : qUnion([Q0, Q1]), "mirrorPlane" : qUnion([Q2])});
        }
        {
            var Q0;
            Q0=makeQuery(id+"F53.opPattern","COPY",FACE,{"derivedFrom":makeQuery(id+"F45.opExtrude","CAP_FACE",FACE,{"disambiguationData":[OSD([sQuery(id+"F44.wireOp",EDGE,"E49"),sQuery(id+"F44.wireOp",EDGE,"E50"),sQuery(id+"F44.wireOp",EDGE,"E51"),sQuery(id+"F44.wireOp",EDGE,"E52")])],"isStart":false}),"instanceName":"1"});
            var sketch = newSketch(context, id + "F54", { "sketchPlane" : qUnion([Q0])});
            skCircle(sketch, "E57", {"center": v(261.58, 239.3) * mm, "radius": 3 * mm});
            skSolve(sketch);
        }
        {
            var Q0;
            Q0 = qSketchRegion(id + "F54", true);
            extrude(context, id + "F55", {"entities" : qUnion([Q0]), "operationType" : NewBodyOperationType.REMOVE, "endBound" : BoundingType.THROUGH_ALL, "oppositeDirection" : true, "depth" : 25 * mm});
        }
        {
            var Q0;
            Q0=makeQuery(id+"F53.opPattern","COPY",FACE,{"derivedFrom":makeQuery(id+"F45.opExtrude","CAP_FACE",FACE,{"disambiguationData":[OSD([sQuery(id+"F44.wireOp",EDGE,"E49"),sQuery(id+"F44.wireOp",EDGE,"E50"),sQuery(id+"F44.wireOp",EDGE,"E51"),sQuery(id+"F44.wireOp",EDGE,"E52")])],"isStart":false}),"instanceName":"1"});
            var sketch = newSketch(context, id + "F56", { "sketchPlane" : qUnion([Q0])});
            skCircle(sketch, "E58.0", {"center": v(261.58, 239.3) * mm, "radius": 3 * mm});
            skSolve(sketch);
        }
        {
            var Q0;
            Q0 = qSketchRegion(id + "F56", true);
            extrude(context, id + "F57", {"entities" : qUnion([Q0]), "oppositeDirection" : true, "depth" : (25 + 2 + 2 + 5) * mm});
        }
        {
            var Q0;
            Q0=makeQuery(id+"F57.opExtrude","CAP_FACE",FACE,{"disambiguationData":[OSD([sQuery(id+"F56.wireOp",EDGE,"E58.0")])],"isStart":true});
            var sketch = newSketch(context, id + "F58", { "sketchPlane" : qUnion([Q0])});
            skCircle(sketch, "E59", {"center": v(261.58, 239.3) * mm, "radius": 7.5 * mm});
            skSolve(sketch);
        }
        {
            var Q0;
            Q0 = qSketchRegion(id + "F58", true);
            extrude(context, id + "F59", {"entities" : qUnion([Q0]), "operationType" : NewBodyOperationType.ADD, "depth" : 10 * mm});
        }
    });
